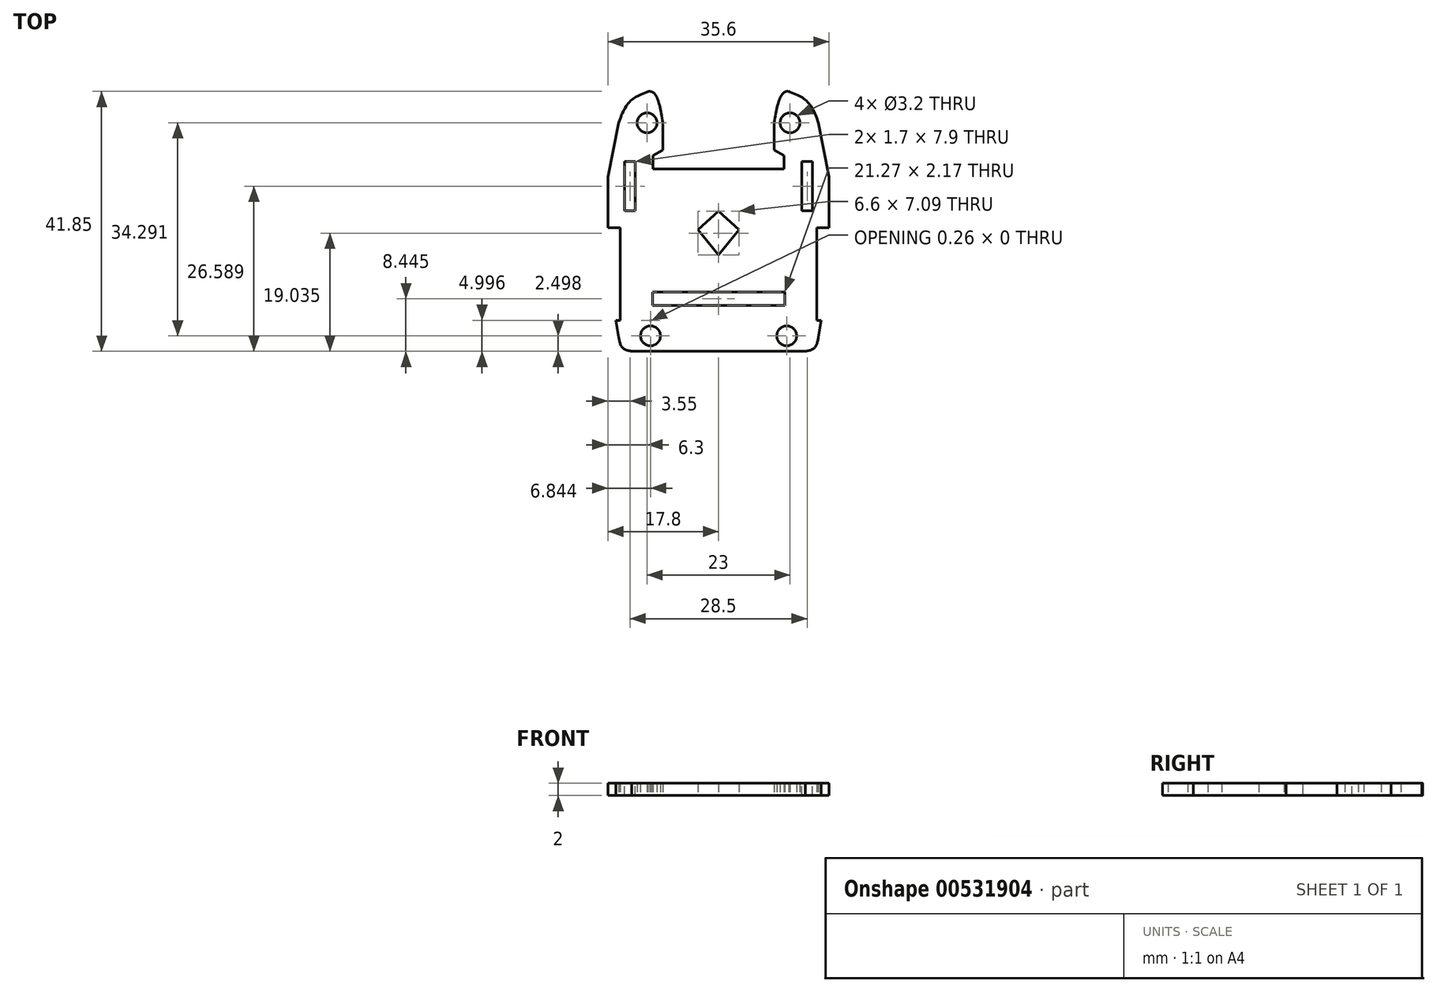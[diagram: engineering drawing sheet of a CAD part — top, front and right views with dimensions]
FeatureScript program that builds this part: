
annotation { "Feature Type Name" : "Feature", "Feature Type Description" : "" }
export const myFeature = defineFeature(function(context is Context, id is Id, definition is map)
    precondition{}
    {
        {
            var Q0;
            Q0=qCreatedBy(makeId("Top.planeOp"),FACE);
            var sketch = newSketch(context, id + "F0", { "sketchPlane" : qUnion([Q0])});
            skPoint(sketch, "E0", {"position": v(10.53, 34.52) * mm});
            skPoint(sketch, "E1", {"position": v(21.97, 0) * mm});
            skPoint(sketch, "E2", {"position": v(22.03, 34.57) * mm});
            skCircle(sketch, "E3", {"center": v(10.53, 34.52) * mm, "radius": 1.6 * mm});
            skPoint(sketch, "E4.endSnap0", {"position": v(0, 17.29) * mm});
            skCircle(sketch, "E5.MirrorC", {"center": v(11.07, 0.23) * mm, "radius": 1.6 * mm});
            skPoint(sketch, "E6", {"position": v(22.03, 17.29) * mm});
            skLineSegment(sketch, "E7", {"start": v(22.03, 13.22) * mm, "end": v(22.03, 7.19) * mm});
            skPoint(sketch, "E8", {"position": v(10.53, 39.5) * mm});
            skPoint(sketch, "E9", {"position": v(5.96, 34.52) * mm});
            skPoint(sketch, "E10", {"position": v(5.97, 0) * mm});
            skLineSegment(sketch, "E11", {"start": v(22.03, 34.57) * mm, "end": v(22.03, 35.26) * mm});
            skPoint(sketch, "E12.MirrorP", {"position": v(33.53, 34.52) * mm});
            skCircle(sketch, "E13.MirrorC", {"center": v(33.53, 34.52) * mm, "radius": 1.6 * mm});
            skCircle(sketch, "E14.MirrorC", {"center": v(32.99, 0.23) * mm, "radius": 1.6 * mm});
            skPoint(sketch, "E15.MirrorP", {"position": v(33.53, 39.5) * mm});
            skPoint(sketch, "E16.MirrorP", {"position": v(38.09, 0) * mm});
            skFitSpline(sketch, "E17", {"points": [v(5.96, 34.52) * mm, v(7.62, 37.8) * mm, v(10.53, 39.5) * mm], "startDerivative": vector(2.52, 7.3) * mm, "endDerivative": vector(7.64, 2.94) * mm});
            skPoint(sketch, "E18.orphan", {"position": v(14.8, 40.62) * mm});
            skPoint(sketch, "E19.MirrorP", {"position": v(29.26, 40.62) * mm});
            skPoint(sketch, "E20", {"position": v(22.03, 28.18) * mm});
            skLineSegment(sketch, "E21.bottom", {"start": v(32.6, 27.1) * mm, "end": v(11.47, 27.1) * mm});
            skLineSegment(sketch, "E21.left", {"start": v(32.6, 27.1) * mm, "end": v(32.6, 29.26) * mm});
            skLineSegment(sketch, "E21.right", {"start": v(11.47, 27.1) * mm, "end": v(11.47, 29.26) * mm});
            skLineSegment(sketch, "E22", {"start": v(22.03, 28.18) * mm, "end": v(22.03, 20.3) * mm});
            skPoint(sketch, "E23", {"position": v(21.96, 6.17) * mm});
            skLineSegment(sketch, "E24.bottom", {"start": v(32.52, 5.09) * mm, "end": v(11.4, 5.09) * mm});
            skLineSegment(sketch, "E24.top", {"start": v(32.52, 7.26) * mm, "end": v(11.4, 7.26) * mm});
            skLineSegment(sketch, "E24.right", {"start": v(11.4, 5.09) * mm, "end": v(11.4, 7.26) * mm});
            skPoint(sketch, "E25.MirrorP", {"position": v(5.97, 17.29) * mm});
            skPoint(sketch, "E26.orphan", {"position": v(4.88, 27.8) * mm});
            skPoint(sketch, "E27.orphan", {"position": v(4.88, 6.77) * mm});
            skPoint(sketch, "E28", {"position": v(11.07, -5.1) * mm});
            skPoint(sketch, "E29.MirrorP", {"position": v(22.09, 0) * mm});
            skPoint(sketch, "E30.MirrorP", {"position": v(32.99, -5.1) * mm});
            skPoint(sketch, "E31.orphan", {"position": v(5.97, -5.1) * mm});
            skPoint(sketch, "E32.MirrorCS.end.orphan", {"position": v(38.09, -5.1) * mm});
            skPoint(sketch, "E33", {"position": v(7.78, 24.32) * mm});
            skLineSegment(sketch, "E34", {"start": v(5.96, 34.52) * mm, "end": v(4.23, 25.82) * mm});
            skPoint(sketch, "E34.endSnap0", {"position": v(5.23, 18.5) * mm});
            skLineSegment(sketch, "E35", {"start": v(5.5, 2.72) * mm, "end": v(5.97, 0) * mm});
            skArc(sketch, "E36.MirrorCS", {"start": v(33.33, 39.56) * mm, "mid": v(33.43, 39.53) * mm, "end": v(33.53, 39.5) * mm});
            skLineSegment(sketch, "E37.MirrorCS", {"start": v(32.66, 5.09) * mm, "end": v(32.66, 7.26) * mm});
            skFitSpline(sketch, "E38.MirrorCS", {"points": [v(38.1, 34.52) * mm, v(36.44, 37.8) * mm, v(33.53, 39.5) * mm], "startDerivative": vector(-2.52, 7.3) * mm, "endDerivative": vector(-7.64, 2.94) * mm});
            skLineSegment(sketch, "E39.MirrorCS", {"start": v(38.1, 34.52) * mm, "end": v(39.83, 25.82) * mm});
            skPoint(sketch, "E40.MirrorP", {"position": v(39.18, 6.77) * mm});
            skLineSegment(sketch, "E41.MirrorCS", {"start": v(11.47, 27.1) * mm, "end": v(32.6, 27.1) * mm});
            skPoint(sketch, "E42.MirrorP", {"position": v(39.18, 27.8) * mm});
            skPoint(sketch, "E43.MirrorP", {"position": v(44.06, 17.29) * mm});
            skLineSegment(sketch, "E44.MirrorCS", {"start": v(38.56, 2.72) * mm, "end": v(38.09, 0) * mm});
            skLineSegment(sketch, "E45.MirrorCS", {"start": v(11.54, 5.09) * mm, "end": v(32.66, 5.09) * mm});
            skLineSegment(sketch, "E46.MirrorCS", {"start": v(11.54, 7.26) * mm, "end": v(32.66, 7.26) * mm});
            skLineSegment(sketch, "E47", {"start": v(39.83, 25.82) * mm, "end": v(39.83, 17.62) * mm});
            skPoint(sketch, "E48.orphan", {"position": v(41.29, 18.5) * mm});
            skLineSegment(sketch, "E49.MirrorCS", {"start": v(6.93, 21.12) * mm, "end": v(7.78, 21.12) * mm});
            skLineSegment(sketch, "E50.MirrorCS", {"start": v(6.93, 27.52) * mm, "end": v(7.78, 27.52) * mm});
            skLineSegment(sketch, "E51.MirrorCS", {"start": v(4.23, 25.82) * mm, "end": v(4.23, 17.62) * mm});
            skPoint(sketch, "E52.MirrorP", {"position": v(2.77, 18.5) * mm});
            skPoint(sketch, "E53.MirrorP", {"position": v(7.78, 19.4) * mm});
            skPoint(sketch, "E54.endSnap0", {"position": v(22.03, 35.8) * mm});
            skPoint(sketch, "E55.orphan", {"position": v(22.03, 37.04) * mm});
            skPoint(sketch, "E56.MirrorCS.end.orphan", {"position": v(28.37, 40.18) * mm});
            skPoint(sketch, "E56.MirrorCS.start.orphan", {"position": v(30.4, 40.37) * mm});
            skPoint(sketch, "E57.end.orphan", {"position": v(15.69, 40.18) * mm});
            skPoint(sketch, "E58.orphan", {"position": v(13.67, 40.37) * mm});
            skLineSegment(sketch, "E59", {"start": v(22.03, 20.3) * mm, "end": v(25.33, 17.29) * mm});
            skLineSegment(sketch, "E60", {"start": v(25.33, 17.29) * mm, "end": v(22.03, 13.22) * mm});
            skLineSegment(sketch, "E61.MirrorCS", {"start": v(18.73, 17.29) * mm, "end": v(22.03, 13.22) * mm});
            skLineSegment(sketch, "E62.MirrorCS", {"start": v(22.03, 20.3) * mm, "end": v(18.73, 17.29) * mm});
            skPoint(sketch, "E63.MirrorP", {"position": v(38.83, 18.5) * mm});
            skLineSegment(sketch, "E64", {"start": v(6.93, 27.52) * mm, "end": v(6.93, 21.12) * mm});
            skLineSegment(sketch, "E65.MirrorCS", {"start": v(8.63, 21.12) * mm, "end": v(7.78, 21.12) * mm});
            skLineSegment(sketch, "E66.MirrorCS", {"start": v(8.63, 27.52) * mm, "end": v(7.78, 27.52) * mm});
            skPoint(sketch, "E67.MirrorP", {"position": v(7.78, 18.5) * mm});
            skLineSegment(sketch, "E68.MirrorCS", {"start": v(8.63, 27.52) * mm, "end": v(8.63, 21.12) * mm});
            skPoint(sketch, "E69.orphan", {"position": v(9.48, 21.12) * mm});
            skPoint(sketch, "E70.orphan", {"position": v(9.48, 27.52) * mm});
            skPoint(sketch, "E71.orphan", {"position": v(6.08, 27.52) * mm});
            skPoint(sketch, "E72.orphan", {"position": v(6.08, 21.12) * mm});
            skPoint(sketch, "E73.MirrorP", {"position": v(36.28, 24.32) * mm});
            skLineSegment(sketch, "E74.MirrorCS", {"start": v(35.43, 27.52) * mm, "end": v(36.28, 27.52) * mm});
            skLineSegment(sketch, "E75.MirrorCS", {"start": v(35.43, 21.12) * mm, "end": v(36.28, 21.12) * mm});
            skLineSegment(sketch, "E76.MirrorCS", {"start": v(37.13, 27.52) * mm, "end": v(36.28, 27.52) * mm});
            skPoint(sketch, "E77.MirrorP", {"position": v(36.28, 19.4) * mm});
            skLineSegment(sketch, "E78.MirrorCS", {"start": v(37.13, 21.12) * mm, "end": v(36.28, 21.12) * mm});
            skPoint(sketch, "E79.MirrorP", {"position": v(36.28, 18.5) * mm});
            skPoint(sketch, "E80.MirrorP", {"position": v(38.09, 17.29) * mm});
            skLineSegment(sketch, "E81.MirrorCS", {"start": v(35.43, 27.52) * mm, "end": v(35.43, 21.12) * mm});
            skPoint(sketch, "E82.MirrorP", {"position": v(34.58, 27.52) * mm});
            skPoint(sketch, "E83.MirrorP", {"position": v(34.58, 21.12) * mm});
            skLineSegment(sketch, "E84.MirrorCS", {"start": v(37.13, 27.52) * mm, "end": v(37.13, 21.12) * mm});
            skPoint(sketch, "E85.MirrorP", {"position": v(37.98, 27.52) * mm});
            skPoint(sketch, "E86.MirrorP", {"position": v(37.98, 21.12) * mm});
            skPoint(sketch, "E87.1.internal.snap0", {"position": v(11.44, 39.78) * mm});
            skFitSpline(sketch, "E87", {"points": [v(9.28, 39.02) * mm, v(11.44, 39.45) * mm, v(13.08, 34.56) * mm], "startDerivative": vector(6.01, 2.9) * mm, "endDerivative": vector(1.87, -10.87) * mm});
            skLineSegment(sketch, "E88", {"start": v(13.08, 34.56) * mm, "end": v(13.08, 30.12) * mm});
            skFitSpline(sketch, "E89.MirrorCS", {"points": [v(34.78, 39.02) * mm, v(32.62, 39.45) * mm, v(30.98, 34.56) * mm], "startDerivative": vector(-6.01, 2.9) * mm, "endDerivative": vector(-1.87, -10.87) * mm});
            skLineSegment(sketch, "E90.MirrorCS", {"start": v(30.98, 34.56) * mm, "end": v(30.98, 30.12) * mm});
            skPoint(sketch, "E91.MirrorCS.start.orphan", {"position": v(11.47, 29.26) * mm});
            skPoint(sketch, "E92.MirrorCS.start.orphan", {"position": v(32.6, 29.26) * mm});
            skLineSegment(sketch, "E93", {"start": v(11.47, 29.26) * mm, "end": v(13.08, 30.12) * mm});
            skPoint(sketch, "E94.MirrorCS.end.orphan", {"position": v(13.08, 29.26) * mm});
            skLineSegment(sketch, "E95.MirrorCS", {"start": v(32.6, 29.26) * mm, "end": v(30.98, 30.12) * mm});
            skPoint(sketch, "E96.trimOffspring.start.orphan", {"position": v(30.98, 29.26) * mm});
            skLineSegment(sketch, "E97", {"start": v(10.53, 39.5) * mm, "end": v(10.63, 39.55) * mm});
            skPoint(sketch, "E98", {"position": v(11.07, -2.27) * mm});
            skLineSegment(sketch, "E99", {"start": v(8.08, -2.27) * mm, "end": v(35.98, -2.27) * mm});
            skFitSpline(sketch, "E100", {"points": [v(5.97, 0) * mm, v(6.57, -1.68) * mm, v(8.08, -2.27) * mm], "startDerivative": vector(0.67, -3.82) * mm, "endDerivative": vector(3.56, -0.7) * mm});
            skFitSpline(sketch, "E101.MirrorCS", {"points": [v(38.09, 0) * mm, v(37.5, -1.68) * mm, v(35.98, -2.27) * mm], "startDerivative": vector(-0.67, -3.82) * mm, "endDerivative": vector(-3.56, -0.7) * mm});
            skPoint(sketch, "E102.MirrorC.center.orphan", {"position": v(32.99, 0) * mm});
            skPoint(sketch, "E103", {"position": v(7.78, 17.62) * mm});
            skArc(sketch, "E104", {"start": v(11.2, 2.72) * mm, "mid": v(11.07, 2.73) * mm, "end": v(10.94, 2.72) * mm});
            skLineSegment(sketch, "E105", {"start": v(11.2, 2.72) * mm, "end": v(10.94, 2.72) * mm});
            skPoint(sketch, "E106", {"position": v(6.23, 17.62) * mm});
            skLineSegment(sketch, "E107.bottom", {"start": v(4.23, 17.62) * mm, "end": v(6.23, 17.62) * mm});
            skLineSegment(sketch, "E107.top", {"start": v(5.5, 2.72) * mm, "end": v(6.23, 2.72) * mm});
            skLineSegment(sketch, "E107.right", {"start": v(6.23, 17.62) * mm, "end": v(6.23, 2.72) * mm});
            skLineSegment(sketch, "E108.MirrorCS", {"start": v(37.83, 17.62) * mm, "end": v(37.83, 2.72) * mm});
            skLineSegment(sketch, "E109.MirrorCS", {"start": v(39.83, 17.62) * mm, "end": v(37.83, 17.62) * mm});
            skLineSegment(sketch, "E110.MirrorCS", {"start": v(38.56, 2.72) * mm, "end": v(37.83, 2.72) * mm});
            skPoint(sketch, "E111.orphan", {"position": v(4.23, 10.08) * mm});
            skPoint(sketch, "E112.orphan", {"position": v(4.23, 2.72) * mm});
            skPoint(sketch, "E113.orphan", {"position": v(39.83, 2.72) * mm});
            skPoint(sketch, "E114.MirrorCS.end.orphan", {"position": v(39.83, 10.08) * mm});
            skPoint(sketch, "E115.orphan", {"position": v(7.02, 2.72) * mm});
            skSolve(sketch);
        }
        {
            var Q0;
            Q0=makeQuery(id+"F0.imprint","IMPRINT",FACE,{"disambiguationData":[TD([[makeQuery(id+"F0.imprint","IMPRINT",EDGE,{"derivedFrom":sQuery(id+"F0.wireOp",EDGE,"E3")}),-1.0]])]});
            extrude(context, id + "F1", {"entities" : qUnion([Q0]), "depth" : 2 * mm, "offsetDistance" : 25 * mm});
        }
        {
            var Q0;
            Q0=makeQuery(id+"F1.opExtrude","CAP_FACE",FACE,{"disambiguationData":[OSD([sQuery(id+"F0.wireOp",EDGE,"E3"),sQuery(id+"F0.wireOp",EDGE,"E5.MirrorC"),sQuery(id+"F0.wireOp",EDGE,"E17"),sQuery(id+"F0.wireOp",EDGE,"E36.MirrorCS"),sQuery(id+"F0.wireOp",EDGE,"E37.MirrorCS"),sQuery(id+"F0.wireOp",EDGE,"E21.left"),sQuery(id+"F0.wireOp",EDGE,"E13.MirrorC"),sQuery(id+"F0.wireOp",EDGE,"E38.MirrorCS"),sQuery(id+"F0.wireOp",EDGE,"E39.MirrorCS"),sQuery(id+"F0.wireOp",EDGE,"E14.MirrorC"),sQuery(id+"F0.wireOp",EDGE,"E44.MirrorCS"),sQuery(id+"F0.wireOp",EDGE,"E47"),sQuery(id+"F0.wireOp",EDGE,"E24.bottom"),sQuery(id+"F0.wireOp",EDGE,"E24.top"),sQuery(id+"F0.wireOp",EDGE,"E45.MirrorCS"),sQuery(id+"F0.wireOp",EDGE,"E24.right"),sQuery(id+"F0.wireOp",EDGE,"E41.MirrorCS"),sQuery(id+"F0.wireOp",EDGE,"E21.right"),sQuery(id+"F0.wireOp",EDGE,"E46.MirrorCS"),sQuery(id+"F0.wireOp",EDGE,"E49.MirrorCS"),sQuery(id+"F0.wireOp",EDGE,"E50.MirrorCS"),sQuery(id+"F0.wireOp",EDGE,"E51.MirrorCS"),sQuery(id+"F0.wireOp",EDGE,"E35"),sQuery(id+"F0.wireOp",EDGE,"E34"),sQuery(id+"F0.wireOp",EDGE,"E59"),sQuery(id+"F0.wireOp",EDGE,"E60"),sQuery(id+"F0.wireOp",EDGE,"E61.MirrorCS"),sQuery(id+"F0.wireOp",EDGE,"E62.MirrorCS"),sQuery(id+"F0.wireOp",EDGE,"E64"),sQuery(id+"F0.wireOp",EDGE,"E65.MirrorCS"),sQuery(id+"F0.wireOp",EDGE,"E66.MirrorCS"),sQuery(id+"F0.wireOp",EDGE,"E68.MirrorCS"),sQuery(id+"F0.wireOp",EDGE,"E74.MirrorCS"),sQuery(id+"F0.wireOp",EDGE,"E75.MirrorCS"),sQuery(id+"F0.wireOp",EDGE,"E76.MirrorCS"),sQuery(id+"F0.wireOp",EDGE,"E78.MirrorCS"),sQuery(id+"F0.wireOp",EDGE,"E81.MirrorCS"),sQuery(id+"F0.wireOp",EDGE,"E84.MirrorCS"),sQuery(id+"F0.wireOp",EDGE,"E87"),sQuery(id+"F0.wireOp",EDGE,"E88"),sQuery(id+"F0.wireOp",EDGE,"E89.MirrorCS"),sQuery(id+"F0.wireOp",EDGE,"E90.MirrorCS"),sQuery(id+"F0.wireOp",EDGE,"E93"),sQuery(id+"F0.wireOp",EDGE,"E95.MirrorCS"),sQuery(id+"F0.wireOp",EDGE,"E97"),sQuery(id+"F0.wireOp",EDGE,"E99"),sQuery(id+"F0.wireOp",EDGE,"E100"),sQuery(id+"F0.wireOp",EDGE,"E101.MirrorCS"),sQuery(id+"F0.wireOp",EDGE,"E104"),sQuery(id+"F0.wireOp",EDGE,"E105"),sQuery(id+"F0.wireOp",EDGE,"E107.bottom"),sQuery(id+"F0.wireOp",EDGE,"E107.top"),sQuery(id+"F0.wireOp",EDGE,"E107.right"),sQuery(id+"F0.wireOp",EDGE,"E108.MirrorCS"),sQuery(id+"F0.wireOp",EDGE,"E109.MirrorCS"),sQuery(id+"F0.wireOp",EDGE,"E110.MirrorCS")])],"isStart":false});
            var sketch = newSketch(context, id + "F2", { "sketchPlane" : qUnion([Q0])});
            skPoint(sketch, "E116", {"position": v(8.63, 28.27) * mm});
            skPoint(sketch, "E117", {"position": v(8.63, 20.37) * mm});
            skPoint(sketch, "E118", {"position": v(6.93, 28.27) * mm});
            skLineSegment(sketch, "E119.bottom", {"start": v(6.93, 28.27) * mm, "end": v(8.63, 28.27) * mm});
            skLineSegment(sketch, "E119.top", {"start": v(6.93, 20.37) * mm, "end": v(8.63, 20.37) * mm});
            skLineSegment(sketch, "E119.left", {"start": v(6.93, 28.27) * mm, "end": v(6.93, 20.37) * mm});
            skLineSegment(sketch, "E119.right", {"start": v(8.63, 28.27) * mm, "end": v(8.63, 20.37) * mm});
            skLineSegment(sketch, "E120", {"start": v(22.03, 27.1) * mm, "end": v(22.03, 31.46) * mm});
            skLineSegment(sketch, "E121.MirrorCS", {"start": v(37.13, 28.27) * mm, "end": v(35.43, 28.27) * mm});
            skPoint(sketch, "E122.MirrorP", {"position": v(35.43, 28.27) * mm});
            skPoint(sketch, "E123.MirrorP", {"position": v(35.43, 20.37) * mm});
            skPoint(sketch, "E124.MirrorP", {"position": v(37.13, 28.27) * mm});
            skLineSegment(sketch, "E125.MirrorCS", {"start": v(35.43, 28.27) * mm, "end": v(35.43, 20.37) * mm});
            skLineSegment(sketch, "E126.MirrorCS", {"start": v(37.13, 28.27) * mm, "end": v(37.13, 20.37) * mm});
            skLineSegment(sketch, "E127.MirrorCS", {"start": v(37.13, 20.37) * mm, "end": v(35.43, 20.37) * mm});
            skSolve(sketch);
        }
        {
            var Q0;
            {var subQ0=sQuery(id+"F2.wireOp",EDGE,"E119.bottom");Q0=makeQuery(id+"F2.imprint","IMPRINT",FACE,{"disambiguationData":[TD([[makeQuery(id+"F2.imprint","IMPRINT",EDGE,{"derivedFrom":subQ0}),-1.0]])]});}
            var Q1;
            {var subQ0=sQuery(id+"F2.wireOp",EDGE,"E119.top");Q1=makeQuery(id+"F2.imprint","IMPRINT",FACE,{"disambiguationData":[TD([[makeQuery(id+"F2.imprint","IMPRINT",EDGE,{"derivedFrom":subQ0}),1.0]])]});}
            var Q2;
            {var subQ0=sQuery(id+"F2.wireOp",EDGE,"E121.MirrorCS");Q2=makeQuery(id+"F2.imprint","IMPRINT",FACE,{"disambiguationData":[TD([[makeQuery(id+"F2.imprint","IMPRINT",EDGE,{"derivedFrom":subQ0}),1.0]])]});}
            var Q3;
            {var subQ2=sQuery(id+"F2.wireOp",EDGE,"E127.MirrorCS");Q3=makeQuery(id+"F2.imprint","IMPRINT",FACE,{"disambiguationData":[TD([[makeQuery(id+"F2.imprint","IMPRINT",EDGE,{"derivedFrom":subQ2}),-1.0]])]});}
            extrude(context, id + "F3", {"entities" : qUnion([Q0, Q1, Q2, Q3]), "operationType" : NewBodyOperationType.REMOVE, "oppositeDirection" : true, "depth" : 25 * mm, "offsetDistance" : 25 * mm});
        }
    });
